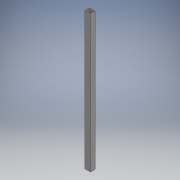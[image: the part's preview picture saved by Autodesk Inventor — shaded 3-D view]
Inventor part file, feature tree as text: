
AUTODESK INVENTOR PART (.ipt)
format: ipt  version: 2016 (Build 200138000, 138)  size: 97,280 bytes
history: native  units: mm
features: extrude x2, sketch x2
ambient origin geometry x8: Origin, YZ Plane, XZ Plane, XY Plane, X Axis, Y Axis, Z Axis, Center Point
bodies: Solid1 (feature_tree)
feature tree (4):
  extrude  "Extrusion1"  Depth=10.0mm
  extrude  "Extrusion3"  Depth=300.0mm TaperAngle=0.0deg
  sketch  "Sketch1"  dims[d0=12.0mm d1=10.0mm]
  sketch  "Sketch3"  dims[d2=300.0mm d3=0.0mm d8=150.0mm d9=0.0mm]
